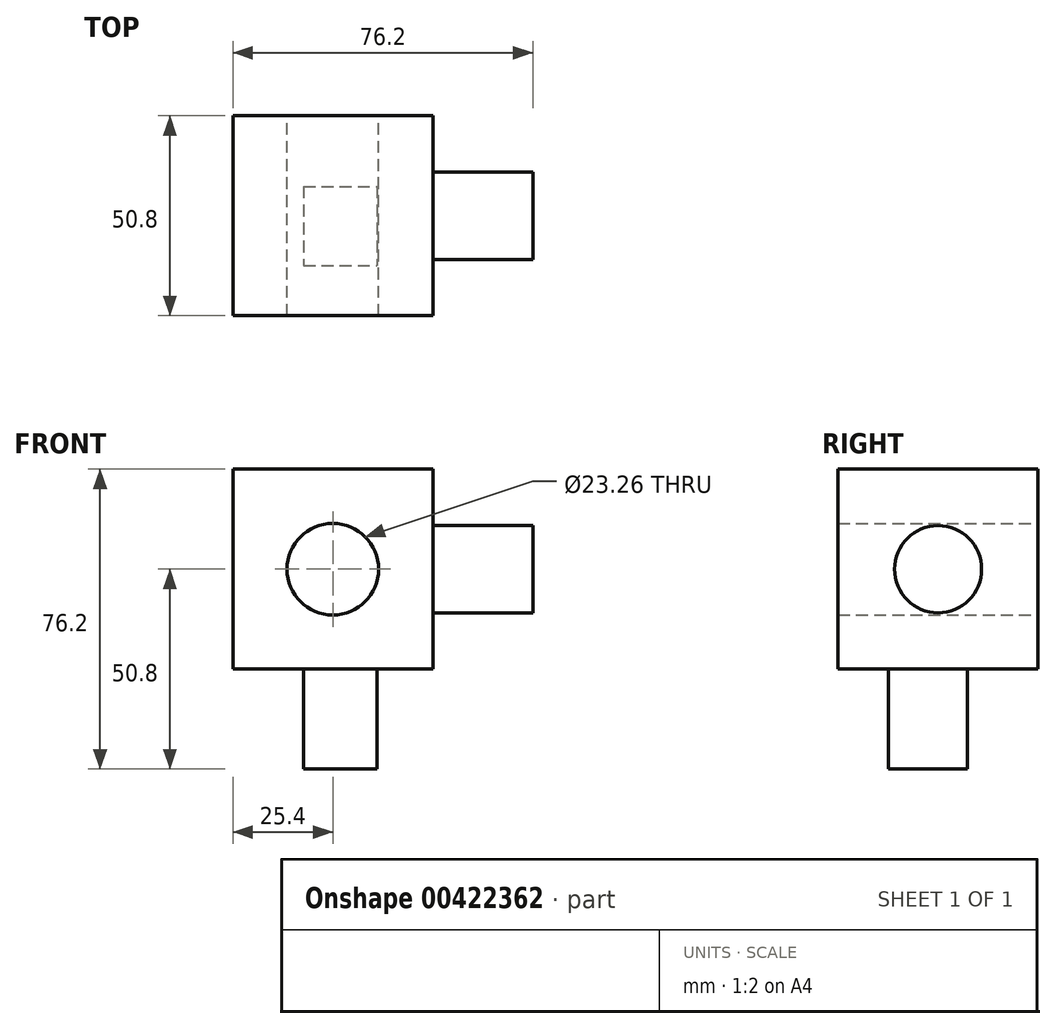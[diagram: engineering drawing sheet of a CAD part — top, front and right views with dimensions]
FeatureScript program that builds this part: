
annotation { "Feature Type Name" : "Feature", "Feature Type Description" : "" }
export const myFeature = defineFeature(function(context is Context, id is Id, definition is map)
    precondition{}
    {
        {
            var Q0;
            Q0=qCreatedBy(makeId("Front.planeOp"),FACE);
            var sketch = newSketch(context, id + "F0", { "sketchPlane" : qUnion([Q0])});
            skLineSegment(sketch, "E0.bottom", {"start": v(0, 0) * mm, "end": v(50.8, 0) * mm});
            skLineSegment(sketch, "E0.top", {"start": v(0, 50.8) * mm, "end": v(50.8, 50.8) * mm});
            skLineSegment(sketch, "E0.left", {"start": v(0, 0) * mm, "end": v(0, 50.8) * mm});
            skLineSegment(sketch, "E0.right", {"start": v(50.8, 0) * mm, "end": v(50.8, 50.8) * mm});
            skCircle(sketch, "E1", {"center": v(25.4, 25.4) * mm, "radius": 11.63 * mm});
            skSolve(sketch);
        }
        {
            var Q0;
            Q0 = qSketchRegion(id + "F0", true);
            extrude(context, id + "F1", {"entities" : qUnion([Q0]), "depth" : 50.8 * mm});
        }
        {
            var Q0;
            Q0=makeQuery(id+"F1.opExtrude","SWEPT_FACE",FACE,{"disambiguationData":[OSD([sQuery(id+"F0.wireOp",EDGE,"E0.bottom")])]});
            var sketch = newSketch(context, id + "F2", { "sketchPlane" : qUnion([Q0])});
            skLineSegment(sketch, "E2.bottom", {"start": v(17.95, 17.95) * mm, "end": v(36.66, 17.95) * mm});
            skLineSegment(sketch, "E2.top", {"start": v(17.95, 38) * mm, "end": v(36.66, 38) * mm});
            skLineSegment(sketch, "E2.left", {"start": v(17.95, 17.95) * mm, "end": v(17.95, 38) * mm});
            skLineSegment(sketch, "E2.right", {"start": v(36.66, 17.95) * mm, "end": v(36.66, 38) * mm});
            skSolve(sketch);
        }
        {
            var Q0;
            Q0 = qSketchRegion(id + "F2", true);
            extrude(context, id + "F3", {"entities" : qUnion([Q0]), "operationType" : NewBodyOperationType.ADD, "depth" : 25.4 * mm});
        }
        {
            var Q0;
            Q0=makeQuery(id+"F1.opExtrude","SWEPT_FACE",FACE,{"disambiguationData":[OSD([sQuery(id+"F0.wireOp",EDGE,"E0.right")])]});
            var sketch = newSketch(context, id + "F4", { "sketchPlane" : qUnion([Q0])});
            skCircle(sketch, "E3", {"center": v(-25.4, 25.4) * mm, "radius": 11.07 * mm});
            skSolve(sketch);
        }
        {
            var Q0;
            Q0 = qSketchRegion(id + "F4", true);
            extrude(context, id + "F5", {"entities" : qUnion([Q0]), "operationType" : NewBodyOperationType.ADD, "depth" : 25.4 * mm});
        }
    });
